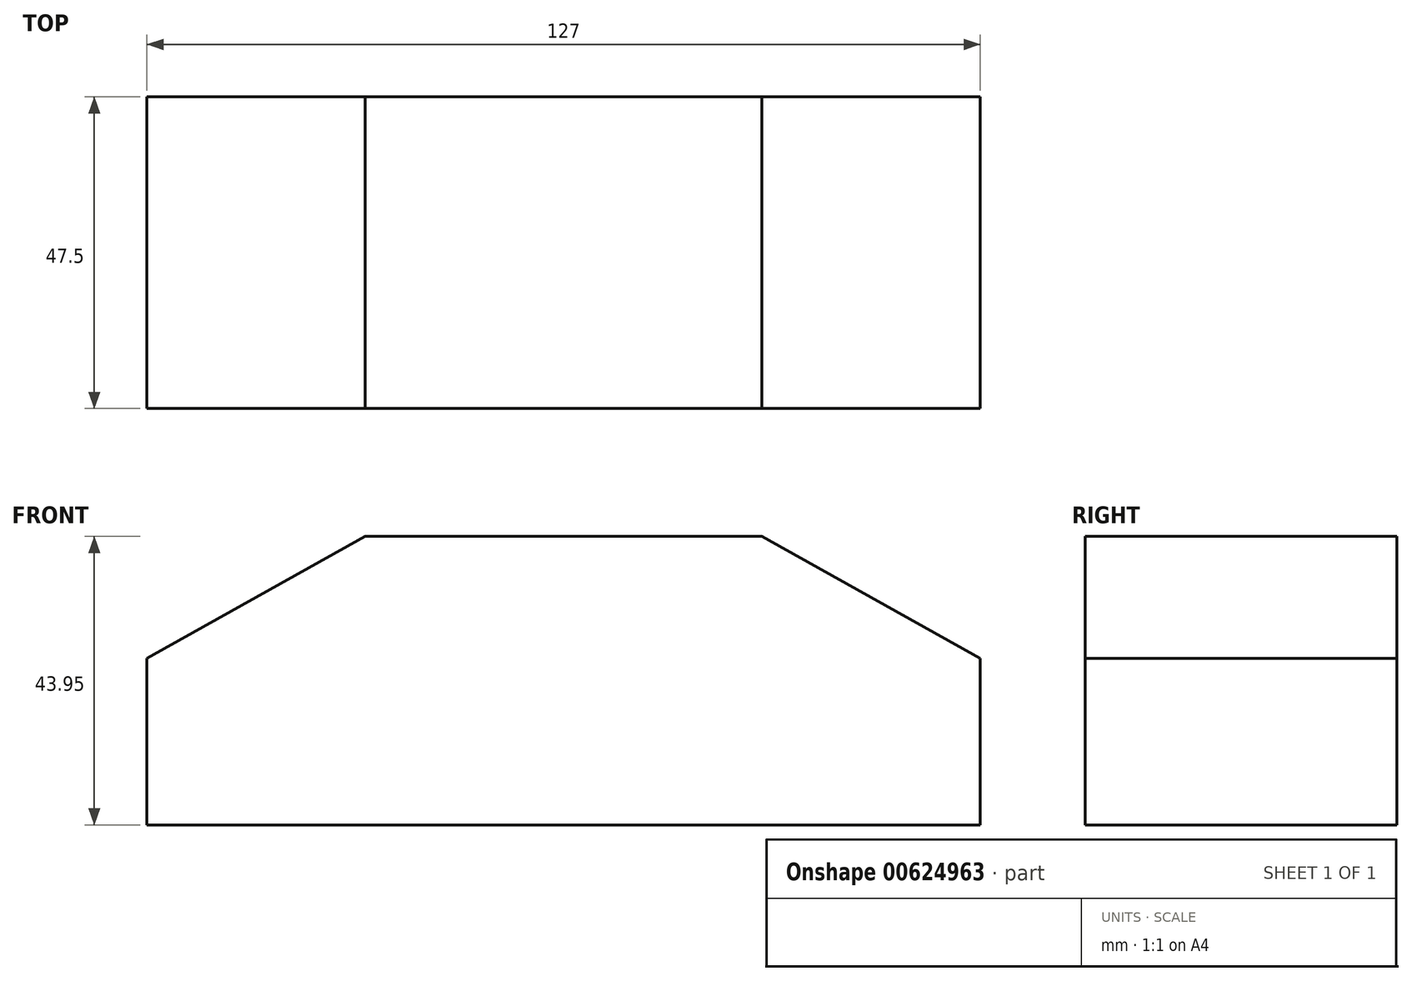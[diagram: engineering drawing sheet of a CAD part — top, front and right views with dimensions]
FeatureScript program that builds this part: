
annotation { "Feature Type Name" : "Feature", "Feature Type Description" : "" }
export const myFeature = defineFeature(function(context is Context, id is Id, definition is map)
    precondition{}
    {
        {
            var Q0;
            Q0=qCreatedBy(makeId("Front.planeOp"),FACE);
            var sketch = newSketch(context, id + "F0", { "sketchPlane" : qUnion([Q0])});
            skLineSegment(sketch, "E0", {"start": v(-66.73, -25.4) * mm, "end": v(60.27, -25.4) * mm});
            skLineSegment(sketch, "E1", {"start": v(60.27, -25.4) * mm, "end": v(60.27, 0) * mm});
            skLineSegment(sketch, "E2", {"start": v(-66.73, -25.4) * mm, "end": v(-66.73, 0) * mm});
            skLineSegment(sketch, "E3", {"start": v(-66.73, 0) * mm, "end": v(-33.45, 18.55) * mm});
            skLineSegment(sketch, "E4", {"start": v(60.27, 0) * mm, "end": v(27, 18.55) * mm});
            skLineSegment(sketch, "E5", {"start": v(-33.45, 18.55) * mm, "end": v(27, 18.55) * mm});
            skSolve(sketch);
        }
        {
            var Q0;
            Q0 = qSketchRegion(id + "F0", true);
            extrude(context, id + "F1", {"entities" : qUnion([Q0]), "depth" : 47.5 * mm, "offsetDistance" : 25.4 * mm});
        }
    });
